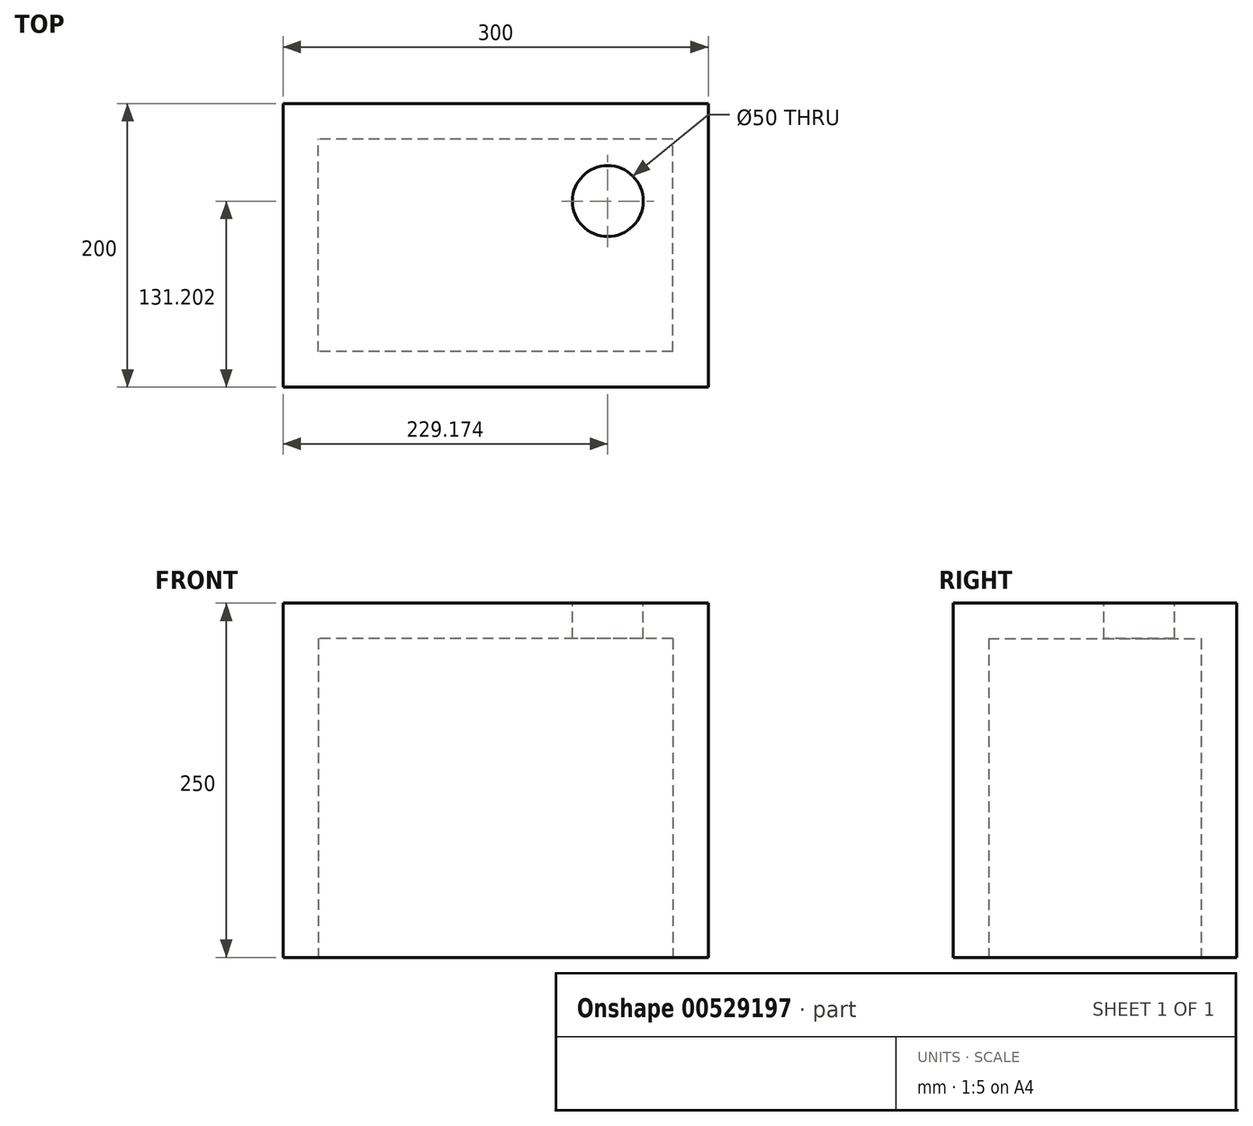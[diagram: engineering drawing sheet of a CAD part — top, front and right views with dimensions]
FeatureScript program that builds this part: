
annotation { "Feature Type Name" : "Feature", "Feature Type Description" : "" }
export const myFeature = defineFeature(function(context is Context, id is Id, definition is map)
    precondition{}
    {
        {
            var Q0;
            Q0=qCreatedBy(makeId("Top.planeOp"),FACE);
            var sketch = newSketch(context, id + "F0", { "sketchPlane" : qUnion([Q0])});
            skLineSegment(sketch, "E0.bottom", {"start": v(150, -100) * mm, "end": v(-150, -100) * mm});
            skLineSegment(sketch, "E0.top", {"start": v(150, 100) * mm, "end": v(-150, 100) * mm});
            skLineSegment(sketch, "E0.left", {"start": v(150, -100) * mm, "end": v(150, 100) * mm});
            skLineSegment(sketch, "E0.right", {"start": v(-150, -100) * mm, "end": v(-150, 100) * mm});
            skPoint(sketch, "E0.middle", {"position": v(0, 0) * mm});
            skSolve(sketch);
        }
        {
            var Q0;
            Q0=makeQuery(id+"F0.imprint","IMPRINT",FACE,{"disambiguationData":[TD([[makeQuery(id+"F0.imprint","IMPRINT",EDGE,{"derivedFrom":sQuery(id+"F0.wireOp",EDGE,"E0.bottom")}),-1.0]])]});
            extrude(context, id + "F1", {"entities" : qUnion([Q0]), "depth" : 250 * mm, "offsetDistance" : 25 * mm});
        }
        {
            var Q0;
            Q0=makeQuery(id+"F1.opExtrude","CAP_FACE",FACE,{"disambiguationData":[OSD([sQuery(id+"F0.wireOp",EDGE,"E0.bottom"),sQuery(id+"F0.wireOp",EDGE,"E0.top"),sQuery(id+"F0.wireOp",EDGE,"E0.left"),sQuery(id+"F0.wireOp",EDGE,"E0.right")])],"isStart":true});
            shell(context, id + "F2", {"entities" : qUnion([Q0]), "thickness" : 25 * mm});
        }
        {
            var Q0;
            Q0=makeQuery(id+"F1.opExtrude","CAP_FACE",FACE,{"disambiguationData":[OSD([sQuery(id+"F0.wireOp",EDGE,"E0.bottom"),sQuery(id+"F0.wireOp",EDGE,"E0.top"),sQuery(id+"F0.wireOp",EDGE,"E0.left"),sQuery(id+"F0.wireOp",EDGE,"E0.right")])],"isStart":false});
            var sketch = newSketch(context, id + "F3", { "sketchPlane" : qUnion([Q0])});
            skCircle(sketch, "E1", {"center": v(79.17, 31.2) * mm, "radius": 45 * mm});
            skSolve(sketch);
        }
        {
            var Q0;
            Q0=sQuery(id+"F3.wireOp",VERTEX,"E1.center");
            var Q1;
            Q1=makeQuery(id+"F1.opExtrude","SWEPT_BODY",BODY,{"disambiguationData":[OSD([sQuery(id+"F0.wireOp",EDGE,"E0.bottom"),sQuery(id+"F0.wireOp",EDGE,"E0.top"),sQuery(id+"F0.wireOp",EDGE,"E0.left"),sQuery(id+"F0.wireOp",EDGE,"E0.right")])]});
            hole(context, id + "F4", {"style" : HoleStyle.SIMPLE, "endStyle" : HoleEndStyle.THROUGH, "holeDiameter" : 50 * mm, "isTappedThrough" : true, "tappedDepth" : 12 * mm, "tapClearance" : 3, "locations" : qUnion([Q0]), "scope" : qUnion([Q1])});
        }
    });
